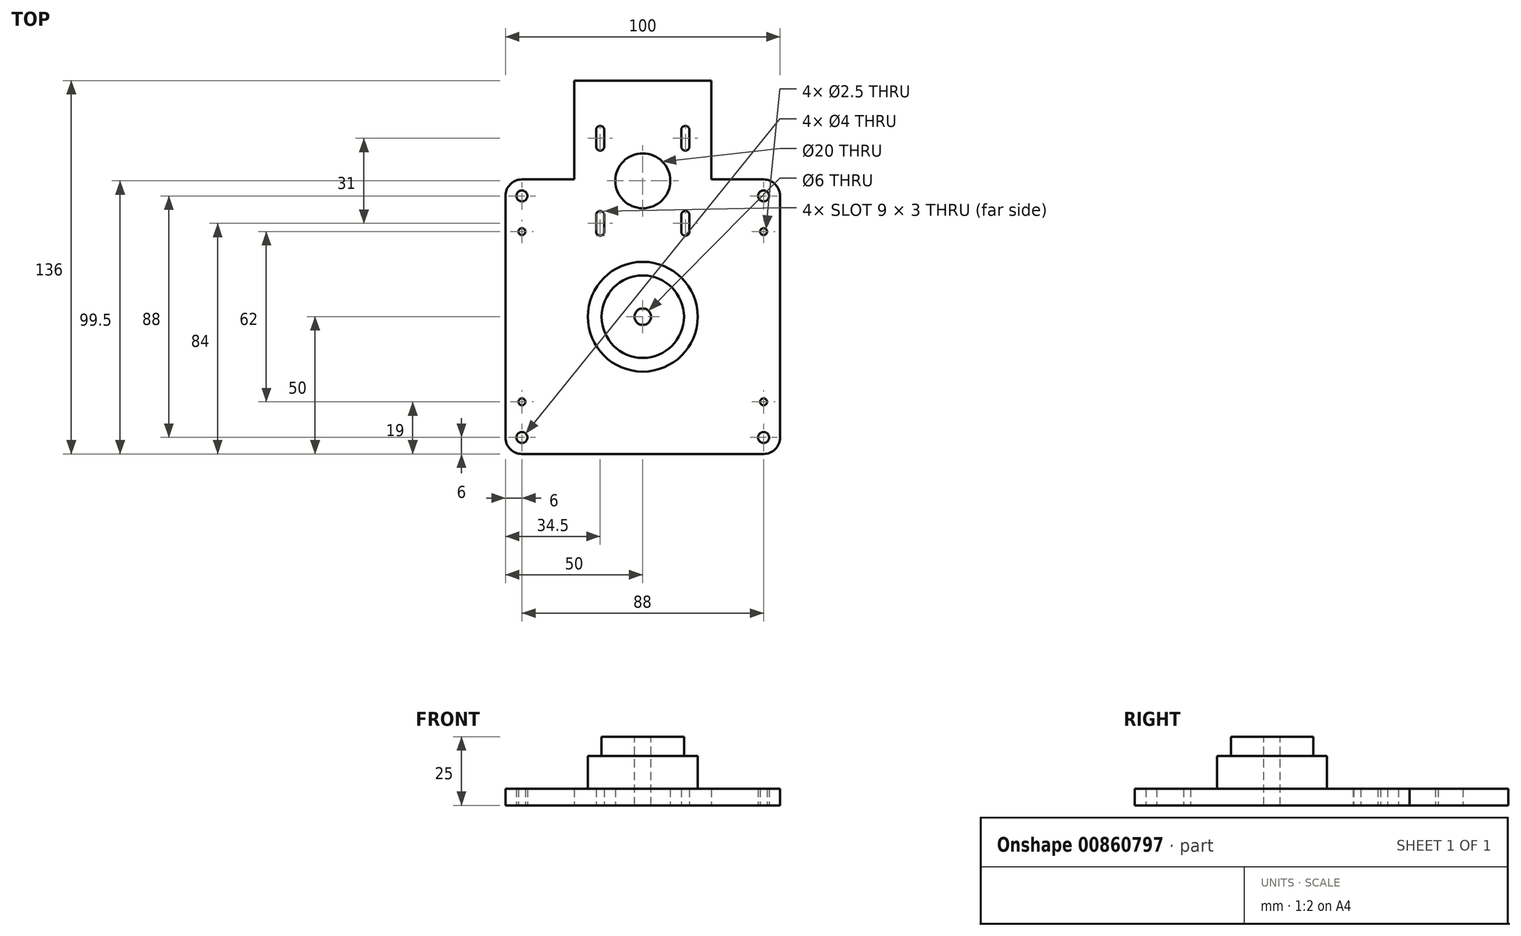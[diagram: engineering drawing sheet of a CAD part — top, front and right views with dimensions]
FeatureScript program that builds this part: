
annotation { "Feature Type Name" : "Feature", "Feature Type Description" : "" }
export const myFeature = defineFeature(function(context is Context, id is Id, definition is map)
    precondition{}
    {
        {
            var Q0;
            Q0=qCreatedBy(makeId("Top.planeOp"),FACE);
            var sketch = newSketch(context, id + "F0", { "sketchPlane" : qUnion([Q0])});
            skLineSegment(sketch, "E0.bottom", {"start": v(6, 0) * mm, "end": v(94, 0) * mm});
            skLineSegment(sketch, "E0.top", {"start": v(6, 100) * mm, "end": v(25, 100) * mm});
            skLineSegment(sketch, "E0.left", {"start": v(0, 6) * mm, "end": v(0, 94) * mm});
            skLineSegment(sketch, "E0.right", {"start": v(100, 6) * mm, "end": v(100, 94) * mm});
            skPoint(sketch, "E1.visualSharp", {"position": v(0, 0) * mm});
            skArc(sketch, "E1.filletArc", {"start": v(0, 6) * mm, "mid": v(1.76, 1.76) * mm, "end": v(6, 0) * mm});
            skPoint(sketch, "E2.visualSharp", {"position": v(100, 0) * mm});
            skArc(sketch, "E2.filletArc", {"start": v(94, 0) * mm, "mid": v(98.24, 1.76) * mm, "end": v(100, 6) * mm});
            skPoint(sketch, "E3.visualSharp", {"position": v(0, 100) * mm});
            skArc(sketch, "E3.filletArc", {"start": v(6, 100) * mm, "mid": v(1.76, 98.24) * mm, "end": v(0, 94) * mm});
            skPoint(sketch, "E4.visualSharp", {"position": v(100, 100) * mm});
            skArc(sketch, "E4.filletArc", {"start": v(100, 94) * mm, "mid": v(98.24, 98.24) * mm, "end": v(94, 100) * mm});
            skLineSegment(sketch, "E5.top", {"start": v(25, 136) * mm, "end": v(75, 136) * mm});
            skLineSegment(sketch, "E5.left", {"start": v(25, 100) * mm, "end": v(25, 136) * mm});
            skLineSegment(sketch, "E5.right", {"start": v(75, 100) * mm, "end": v(75, 136) * mm});
            skLineSegment(sketch, "E6.trimOffspring", {"start": v(75, 100) * mm, "end": v(94, 100) * mm});
            skCircle(sketch, "E7", {"center": v(50, 99.5) * mm, "radius": 10 * mm});
            skPoint(sketch, "E7.centerSnap0", {"position": v(50, 136) * mm});
            skPoint(sketch, "E8", {"position": v(50, 50) * mm});
            skPoint(sketch, "E8.positionSnap0", {"position": v(50, 0) * mm});
            skPoint(sketch, "E8.positionSnap1", {"position": v(0, 50) * mm});
            skLineSegment(sketch, "E9.left", {"start": v(33, 112) * mm, "end": v(33, 118) * mm});
            skLineSegment(sketch, "E9.right", {"start": v(36, 112) * mm, "end": v(36, 118) * mm});
            skLineSegment(sketch, "E10", {"start": v(50, 99.5) * mm, "end": v(50, 123) * mm, "construction": true});
            skLineSegment(sketch, "E11", {"start": v(50, 99.5) * mm, "end": v(33.46, 99.5) * mm, "construction": true});
            skArc(sketch, "E12", {"start": v(36, 118) * mm, "mid": v(34.5, 119.5) * mm, "end": v(33, 118) * mm});
            skArc(sketch, "E13", {"start": v(33, 112) * mm, "mid": v(34.5, 110.5) * mm, "end": v(36, 112) * mm});
            skLineSegment(sketch, "E14.MirrorCS", {"start": v(64, 112) * mm, "end": v(64, 118) * mm});
            skArc(sketch, "E15.MirrorCS", {"start": v(64, 118) * mm, "mid": v(65.5, 119.5) * mm, "end": v(67, 118) * mm});
            skLineSegment(sketch, "E16.MirrorCS", {"start": v(67, 112) * mm, "end": v(67, 118) * mm});
            skArc(sketch, "E17.MirrorCS", {"start": v(67, 112) * mm, "mid": v(65.5, 110.5) * mm, "end": v(64, 112) * mm});
            skArc(sketch, "E18.MirrorCS", {"start": v(33, 87) * mm, "mid": v(34.5, 88.5) * mm, "end": v(36, 87) * mm});
            skLineSegment(sketch, "E19.MirrorCS", {"start": v(33, 87) * mm, "end": v(33, 81) * mm});
            skLineSegment(sketch, "E20.MirrorCS", {"start": v(36, 87) * mm, "end": v(36, 81) * mm});
            skArc(sketch, "E21.MirrorCS", {"start": v(36, 81) * mm, "mid": v(34.5, 79.5) * mm, "end": v(33, 81) * mm});
            skLineSegment(sketch, "E22.MirrorCS", {"start": v(64, 87) * mm, "end": v(64, 81) * mm});
            skArc(sketch, "E23.MirrorCS", {"start": v(64, 81) * mm, "mid": v(65.5, 79.5) * mm, "end": v(67, 81) * mm});
            skLineSegment(sketch, "E24.MirrorCS", {"start": v(67, 87) * mm, "end": v(67, 81) * mm});
            skArc(sketch, "E25.MirrorCS", {"start": v(67, 87) * mm, "mid": v(65.5, 88.5) * mm, "end": v(64, 87) * mm});
            skCircle(sketch, "E26", {"center": v(94, 94) * mm, "radius": 2 * mm});
            skCircle(sketch, "E27", {"center": v(6, 94) * mm, "radius": 2 * mm});
            skCircle(sketch, "E28", {"center": v(94, 6) * mm, "radius": 2 * mm});
            skCircle(sketch, "E29", {"center": v(6, 6) * mm, "radius": 2 * mm});
            skCircle(sketch, "E30", {"center": v(94, 81) * mm, "radius": 1.25 * mm});
            skCircle(sketch, "E31", {"center": v(94, 19) * mm, "radius": 1.25 * mm});
            skLineSegment(sketch, "E32", {"start": v(50, 50) * mm, "end": v(50, 65.58) * mm, "construction": true});
            skCircle(sketch, "E33.MirrorC", {"center": v(6, 81) * mm, "radius": 1.25 * mm});
            skCircle(sketch, "E34.MirrorC", {"center": v(6, 19) * mm, "radius": 1.25 * mm});
            skSolve(sketch);
        }
        {
            var Q0;
            Q0=makeQuery(id+"F0.imprint","IMPRINT",FACE,{"disambiguationData":[TD([[makeQuery(id+"F0.imprint","IMPRINT",EDGE,{"derivedFrom":sQuery(id+"F0.wireOp",EDGE,"E0.bottom")}),1.0]])]});
            extrude(context, id + "F1", {"entities" : qUnion([Q0]), "depth" : 6 * mm, "offsetDistance" : 25 * mm});
        }
        {
            var Q0;
            Q0=makeQuery(id+"F1.opExtrude","CAP_FACE",FACE,{"disambiguationData":[OSD([sQuery(id+"F0.wireOp",EDGE,"E0.bottom"),sQuery(id+"F0.wireOp",EDGE,"E0.top"),sQuery(id+"F0.wireOp",EDGE,"E0.left"),sQuery(id+"F0.wireOp",EDGE,"E0.right"),sQuery(id+"F0.wireOp",EDGE,"E1.filletArc"),sQuery(id+"F0.wireOp",EDGE,"E2.filletArc"),sQuery(id+"F0.wireOp",EDGE,"E3.filletArc"),sQuery(id+"F0.wireOp",EDGE,"E4.filletArc"),sQuery(id+"F0.wireOp",EDGE,"E5.top"),sQuery(id+"F0.wireOp",EDGE,"E5.left"),sQuery(id+"F0.wireOp",EDGE,"E5.right"),sQuery(id+"F0.wireOp",EDGE,"E6.trimOffspring"),sQuery(id+"F0.wireOp",EDGE,"E7"),sQuery(id+"F0.wireOp",EDGE,"E9.left"),sQuery(id+"F0.wireOp",EDGE,"E9.right"),sQuery(id+"F0.wireOp",EDGE,"E12"),sQuery(id+"F0.wireOp",EDGE,"E13"),sQuery(id+"F0.wireOp",EDGE,"E14.MirrorCS"),sQuery(id+"F0.wireOp",EDGE,"E15.MirrorCS"),sQuery(id+"F0.wireOp",EDGE,"E16.MirrorCS"),sQuery(id+"F0.wireOp",EDGE,"E17.MirrorCS"),sQuery(id+"F0.wireOp",EDGE,"E18.MirrorCS"),sQuery(id+"F0.wireOp",EDGE,"E19.MirrorCS"),sQuery(id+"F0.wireOp",EDGE,"E20.MirrorCS"),sQuery(id+"F0.wireOp",EDGE,"E21.MirrorCS"),sQuery(id+"F0.wireOp",EDGE,"E22.MirrorCS"),sQuery(id+"F0.wireOp",EDGE,"E23.MirrorCS"),sQuery(id+"F0.wireOp",EDGE,"E24.MirrorCS"),sQuery(id+"F0.wireOp",EDGE,"E25.MirrorCS"),sQuery(id+"F0.wireOp",EDGE,"E26"),sQuery(id+"F0.wireOp",EDGE,"E27"),sQuery(id+"F0.wireOp",EDGE,"E28"),sQuery(id+"F0.wireOp",EDGE,"E29"),sQuery(id+"F0.wireOp",EDGE,"E30"),sQuery(id+"F0.wireOp",EDGE,"E31")])],"isStart":false});
            var sketch = newSketch(context, id + "F2", { "sketchPlane" : qUnion([Q0])});
            skCircle(sketch, "E35", {"center": v(50, 50) * mm, "radius": 20 * mm});
            skPoint(sketch, "E35.centerSnap0", {"position": v(50, 0) * mm});
            skPoint(sketch, "E35.centerSnap1", {"position": v(0, 50) * mm});
            skSolve(sketch);
        }
        {
            var Q0;
            Q0 = qSketchRegion(id + "F2", true);
            extrude(context, id + "F3", {"entities" : qUnion([Q0]), "operationType" : NewBodyOperationType.ADD, "depth" : 12 * mm, "offsetDistance" : 25 * mm});
        }
        {
            var Q0;
            Q0=makeQuery(id+"F3.opExtrude","CAP_FACE",FACE,{"disambiguationData":[OSD([sQuery(id+"F2.wireOp",EDGE,"E35")])],"isStart":false});
            var sketch = newSketch(context, id + "F4", { "sketchPlane" : qUnion([Q0])});
            skCircle(sketch, "E36", {"center": v(50, 50) * mm, "radius": 15 * mm});
            skSolve(sketch);
        }
        {
            var Q0;
            Q0 = qSketchRegion(id + "F4", true);
            extrude(context, id + "F5", {"entities" : qUnion([Q0]), "operationType" : NewBodyOperationType.ADD, "depth" : 7 * mm, "offsetDistance" : 25 * mm});
        }
        {
            var Q0;
            Q0=makeQuery(id+"F5.opExtrude","CAP_FACE",FACE,{"disambiguationData":[OSD([sQuery(id+"F4.wireOp",EDGE,"E36")])],"isStart":false});
            var sketch = newSketch(context, id + "F6", { "sketchPlane" : qUnion([Q0])});
            skCircle(sketch, "E37", {"center": v(50, 50) * mm, "radius": 3 * mm});
            skSolve(sketch);
        }
        {
            var Q0;
            Q0 = qSketchRegion(id + "F6", true);
            extrude(context, id + "F7", {"entities" : qUnion([Q0]), "operationType" : NewBodyOperationType.REMOVE, "endBound" : BoundingType.THROUGH_ALL, "oppositeDirection" : true, "depth" : 25 * mm, "offsetDistance" : 25 * mm});
        }
    });
